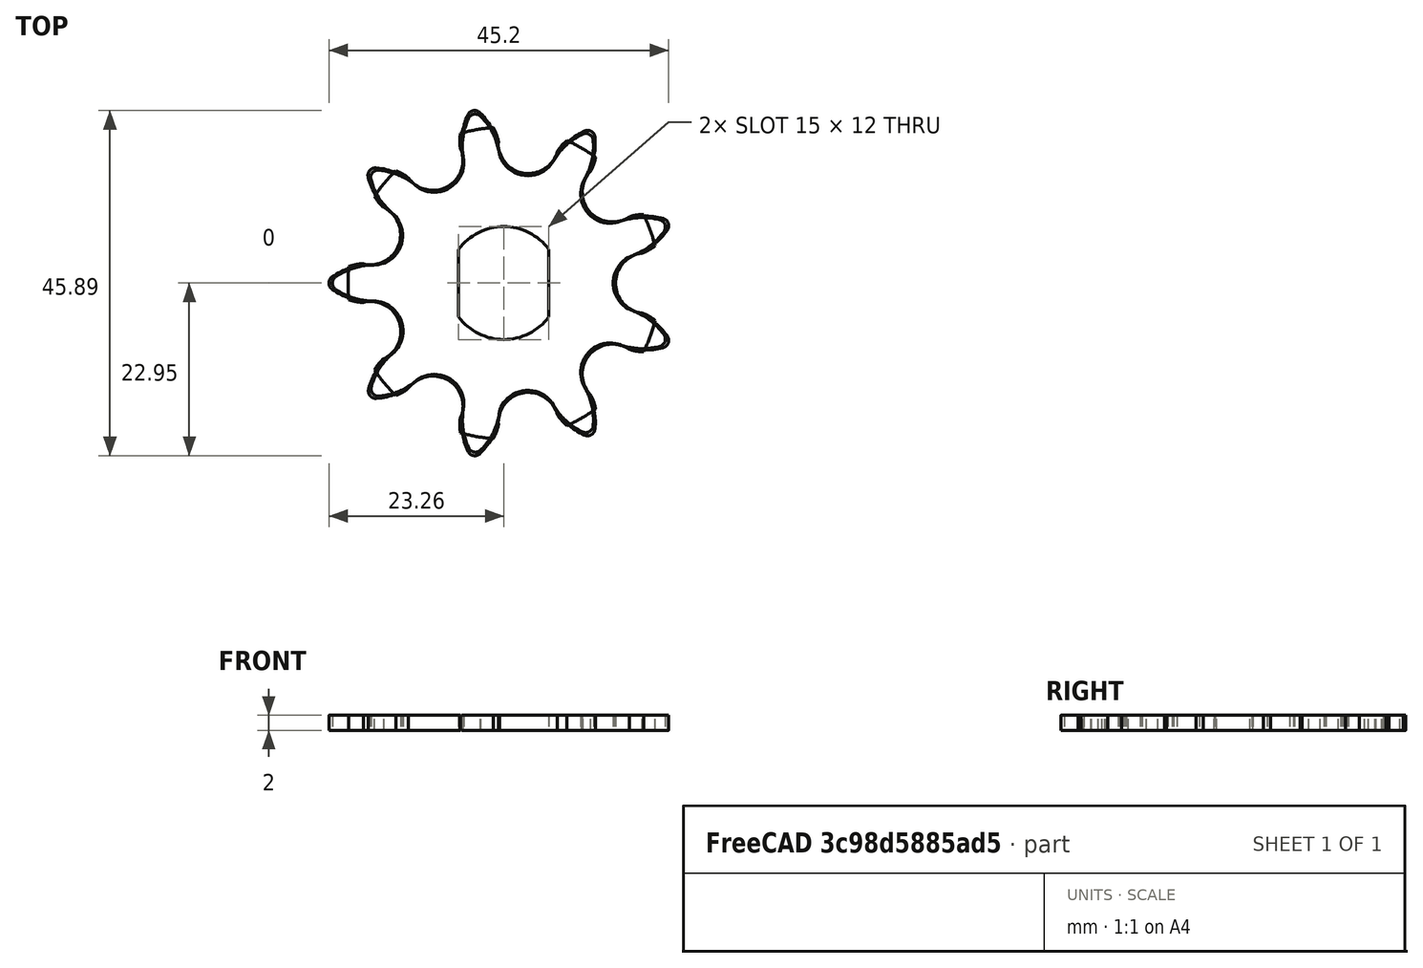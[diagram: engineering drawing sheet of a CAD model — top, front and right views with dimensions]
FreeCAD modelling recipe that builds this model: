
FCSTD DOCUMENT  (FreeCAD 0.21R33771 (Git))
Label: Звезда
License: All rights reserved
LicenseURL: http://en.wikipedia.org/wiki/All_rights_reserved
objects: Part::Cut×4, Part::Box×2, Part::FeaturePython×2, Part::Cylinder×1, Part::MultiFuse×1, Sketcher::SketchObject×1, PartDesign::Pad×1, PartDesign::Body×1, Part::Feature×1
note: 15 computed .brp shape members not serialized (recipe doc carries the construction recipe); baked Part::Feature solids carry a one-line shape summary decoded from their .brp

FEATURE [Part::Cylinder] Cylinder  label="Цилиндр"
  Angle = 360
  AttacherType = Attacher::AttachEngine3D
  FirstAngle = 0
  Height = 2
  Radius = 7.5
  SecondAngle = 0
FEATURE [Part::Box] Box  label="Куб"
  AttacherType = Attacher::AttachEngine3D
  Height = 3
  Length = 2
  Placement = pos=(6,-7.5,0) rot=(0,0,1;0rad)
  Width = 15
FEATURE [Part::Box] Box001  label="Куб001"
  AttacherType = Attacher::AttachEngine3D
  Height = 3
  Length = 2
  Placement = pos=(-8,-7.5,0) rot=(0,0,1;0rad)
  Width = 15
FEATURE [Part::MultiFuse] Fusion
  Refine = true
  Shapes = -> [Box,Box001]
FEATURE [Part::Cut] Cut
  Base = -> Cylinder
  Refine = true
  Tool = -> Fusion
FEATURE [Part::FeaturePython] LanternGear  # WARN: FeaturePython — macro-defined, semantics opaque (R4)
  AttacherType = Attacher::AttachEngine3D
  bolt_radius = 4
  head = -0.5
  height = 2
  module = 4.18
  num_profiles = 10
  teeth = 9
  version = 1.2.0
FEATURE [Part::Cut] Cut001
  Base = -> LanternGear
  Refine = true
  Tool = -> Cut
FEATURE [Sketcher::SketchObject] Sketch
  FullyConstrained = false
  MapMode = 5
  Support = -> [XY_Plane]
  sketch-geometry (36):
    g0: ArcOfCircle CenterX=18.8521 CenterY=-0.00307638 CenterZ=0 NormalX=0 NormalY=0 NormalZ=1 AngleXU=0 Radius=3.99594 StartAngle=1.92021 EndAngle=4.36364
    g1: ArcOfCircle CenterX=14.4427 CenterY=12.1214 CenterZ=0 NormalX=0 NormalY=0 NormalZ=1 AngleXU=0 Radius=3.99956 StartAngle=2.61807 EndAngle=5.06145
    g2: ArcOfCircle CenterX=3.27375 CenterY=18.5664 CenterZ=0 NormalX=0 NormalY=0 NormalZ=1 AngleXU=0 Radius=4.00007 StartAngle=3.31592 EndAngle=5.76013
    g3: ArcOfCircle CenterX=-9.4255 CenterY=16.3265 CenterZ=0 NormalX=0 NormalY=0 NormalZ=1 AngleXU=0 Radius=3.99916 StartAngle=4.01407 EndAngle=6.45773
    g4: ArcOfCircle CenterX=-17.7189 CenterY=6.45012 CenterZ=0 NormalX=0 NormalY=0 NormalZ=1 AngleXU=0 Radius=3.99935 StartAngle=4.71461 EndAngle=7.15498
    g5: ArcOfCircle CenterX=-17.713 CenterY=-6.48365 CenterZ=0 NormalX=0 NormalY=0 NormalZ=1 AngleXU=0 Radius=4.03982 StartAngle=5.41203 EndAngle=7.85425
    g6: ArcOfCircle CenterX=-9.40813 CenterY=-16.3627 CenterZ=0 NormalX=0 NormalY=0 NormalZ=1 AngleXU=0 Radius=3.99368 StartAngle=6.12296 EndAngle=8.55045
    g7: ArcOfCircle CenterX=3.26409 CenterY=-18.5325 CenterZ=0 NormalX=0 NormalY=0 NormalZ=1 AngleXU=0 Radius=3.9982 StartAngle=0.520185 EndAngle=2.87441
    g8: ArcOfCircle CenterX=14.4386 CenterY=-12.1181 CenterZ=0 NormalX=0 NormalY=0 NormalZ=1 AngleXU=0 Radius=4.00046 StartAngle=1.22083 EndAngle=3.66684
    g9: ArcOfCircle CenterX=18.8521 CenterY=-1.6e-15 CenterZ=0 NormalX=0 NormalY=0 NormalZ=1 AngleXU=0 Radius=8.89636 StartAngle=4.36343 EndAngle=4.97952
    g10: ArcOfCircle CenterX=14.4423 CenterY=12.1192 CenterZ=0 NormalX=0 NormalY=0 NormalZ=1 AngleXU=0 Radius=8.9035 StartAngle=5.06105 EndAngle=5.67731
    g11: ArcOfCircle CenterX=3.27349 CenterY=18.5668 CenterZ=0 NormalX=0 NormalY=0 NormalZ=1 AngleXU=0 Radius=8.89593 StartAngle=5.75987 EndAngle=6.37643
    g12: ArcOfCircle CenterX=-9.42653 CenterY=16.3272 CenterZ=0 NormalX=0 NormalY=0 NormalZ=1 AngleXU=0 Radius=8.8961 StartAngle=0.174603 EndAngle=0.781513
    g13: ArcOfCircle CenterX=-17.7173 CenterY=6.44109 CenterZ=0 NormalX=0 NormalY=0 NormalZ=1 AngleXU=0 Radius=8.90336 StartAngle=0.873017 EndAngle=1.48801
    g14: ArcOfCircle CenterX=-17.6902 CenterY=-6.46089 CenterZ=0 NormalX=0 NormalY=0 NormalZ=1 AngleXU=0 Radius=8.91169 StartAngle=1.57302 EndAngle=2.18686
    g15: ArcOfCircle CenterX=-9.39599 CenterY=-16.3607 CenterZ=0 NormalX=0 NormalY=0 NormalZ=1 AngleXU=0 Radius=8.87254 StartAngle=2.27075 EndAngle=2.88286
    g16: ArcOfCircle CenterX=3.28393 CenterY=-18.5776 CenterZ=0 NormalX=0 NormalY=0 NormalZ=1 AngleXU=0 Radius=8.89064 StartAngle=2.96319 EndAngle=3.58322
    g17: ArcOfCircle CenterX=14.4506 CenterY=-12.1215 CenterZ=0 NormalX=0 NormalY=0 NormalZ=1 AngleXU=0 Radius=8.89511 StartAngle=3.6621 EndAngle=4.27987
    g18: ArcOfCircle CenterX=-17.7165 CenterY=6.44925 CenterZ=0 NormalX=0 NormalY=0 NormalZ=1 AngleXU=0 Radius=8.89308 StartAngle=4.09873 EndAngle=4.71266
    g19: ArcOfCircle CenterX=-9.42653 CenterY=16.3272 CenterZ=0 NormalX=0 NormalY=0 NormalZ=1 AngleXU=0 Radius=8.8972 StartAngle=3.39892 EndAngle=4.01426
    g20: ArcOfCircle CenterX=3.27349 CenterY=18.5668 CenterZ=0 NormalX=0 NormalY=0 NormalZ=1 AngleXU=0 Radius=8.89593 StartAngle=2.70052 EndAngle=3.31624
    g21: ArcOfCircle CenterX=14.4423 CenterY=12.1192 CenterZ=0 NormalX=0 NormalY=0 NormalZ=1 AngleXU=0 Radius=8.89579 StartAngle=2.0205 EndAngle=2.61784
    g22: ArcOfCircle CenterX=18.8521 CenterY=1.2e-15 CenterZ=0 NormalX=0 NormalY=0 NormalZ=1 AngleXU=0 Radius=8.89894 StartAngle=1.30342 EndAngle=1.91961
    g23: ArcOfCircle CenterX=14.4506 CenterY=-12.1215 CenterZ=0 NormalX=0 NormalY=0 NormalZ=1 AngleXU=0 Radius=8.89704 StartAngle=0.607101 EndAngle=1.22256
    g24: ArcOfCircle CenterX=3.28393 CenterY=-18.5776 CenterZ=0 NormalX=0 NormalY=0 NormalZ=1 AngleXU=0 Radius=8.88949 StartAngle=6.19282 EndAngle=6.80792
    g25: ArcOfCircle CenterX=-9.39599 CenterY=-16.3607 CenterZ=0 NormalX=0 NormalY=0 NormalZ=1 AngleXU=0 Radius=8.87421 StartAngle=5.49392 EndAngle=6.15708
    g26: ArcOfCircle CenterX=-17.6902 CenterY=-6.46089 CenterZ=0 NormalX=0 NormalY=0 NormalZ=1 AngleXU=0 Radius=8.91523 StartAngle=4.79888 EndAngle=5.40899
    g27: ArcOfCircle CenterX=-17.0637 CenterY=14.3174 CenterZ=0 NormalX=0 NormalY=0 NormalZ=1 AngleXU=0 Radius=1 StartAngle=1.48801 EndAngle=3.39892
    g28: ArcOfCircle CenterX=-3.86675 CenterY=21.9376 CenterZ=0 NormalX=0 NormalY=0 NormalZ=1 AngleXU=0 Radius=1 StartAngle=0.714992 EndAngle=2.70052
    g29: ArcOfCircle CenterX=11.1351 CenterY=19.3019 CenterZ=0 NormalX=0 NormalY=0 NormalZ=1 AngleXU=0 Radius=1 StartAngle=0.0932401 EndAngle=2.16499
    g30: ArcOfCircle CenterX=20.939 CenterY=7.61827 CenterZ=0 NormalX=0 NormalY=0 NormalZ=1 AngleXU=0 Radius=1 StartAngle=5.67731 EndAngle=7.58661
    g31: ArcOfCircle CenterX=20.9364 CenterY=-7.6163 CenterZ=0 NormalX=0 NormalY=0 NormalZ=1 AngleXU=0 Radius=1 StartAngle=4.97952 EndAngle=6.89029
    g32: ArcOfCircle CenterX=11.1412 CenterY=-19.2895 CenterZ=0 NormalX=0 NormalY=0 NormalZ=1 AngleXU=0 Radius=1 StartAngle=4.27987 EndAngle=6.19282
    g33: ArcOfCircle CenterX=-3.84965 CenterY=-21.9501 CenterZ=0 NormalX=0 NormalY=0 NormalZ=1 AngleXU=0 Radius=1 StartAngle=3.58322 EndAngle=5.49392
    g34: ArcOfCircle CenterX=-17.0065 CenterY=-14.3465 CenterZ=0 NormalX=0 NormalY=0 NormalZ=1 AngleXU=0 Radius=1 StartAngle=2.88286 EndAngle=4.79888
    g35: ArcOfCircle CenterX=-22.2618 CenterY=-0.00369913 CenterZ=0 NormalX=0 NormalY=0 NormalZ=1 AngleXU=0 Radius=1 StartAngle=2.18686 EndAngle=4.09873
  constraints (44):
    c: Coincident(g0,g23)
    c: Coincident(g8,g9)
    c: Coincident(g8,g24)
    c: Coincident(g7,g17)
    c: Coincident(g7,g25)
    c: Coincident(g6,g16)
    c: Coincident(g6,g26)
    c: Coincident(g5,g15)
    c: Coincident(g5,g18)
    c: Coincident(g4,g14)
    c: Coincident(g4,g19)
    c: Coincident(g3,g13)
    c: Coincident(g3,g20)
    c: Coincident(g2,g12)
    c: Coincident(g2,g21)
    c: Coincident(g1,g11)
    c: Coincident(g1,g22)
    c: Coincident(g0,g10)
    c: Diameter(g27) = 2
    c: Equal(g27,g28) = 2
    c: Tangent(g27,g19) = -1.5708
    c: Tangent(g27,g13) = -1.5708
    c: Tangent(g28,g20) = -1.5708
    c: Coincident(g28,g12)
    c: Coincident(g29,g21)
    c: Tangent(g11,g29) = -1.5708
    c: Diameter(g30) = 2
    c: Equal(g30,g31) = 2
    c: Equal(g30,g32) = 2
    c: Equal(g30,g33) = 2
    c: Equal(g30,g34) = 2
    c: Equal(g30,g35) = 2
    c: Tangent(g35,g18) = -1.5708
    c: Tangent(g35,g14) = -1.5708
    c: Tangent(g34,g26) = -1.5708
    c: Tangent(g34,g15) = -1.5708
    c: Tangent(g33,g25) = -1.5708
    c: Tangent(g33,g16) = -1.5708
    c: Tangent(g32,g24) = -1.5708
    c: Tangent(g32,g17) = -1.5708
    c: Tangent(g31,g23) = -1.5708
    c: Tangent(g31,g9) = -1.5708
    c: Tangent(g10,g30) = -1.5708
    c: Tangent(g22,g30) = -1.5708
FEATURE [PartDesign::Pad] Pad
  Direction = (0,0,1)
  Length = 2
  Length2 = 10
  Profile = -> Sketch
  ReferenceAxis = -> Sketch [N_Axis]
  Refine = true
  Type = 0
FEATURE [PartDesign::Body] Body
  Group = -> [Sketch,Pad]
  Origin = -> Origin
  Tip = -> Pad
FEATURE [Part::Cut] Cut002
  Base = -> Body
  Refine = true
  Tool = -> Cut
FEATURE [Part::Feature] Body001
  shape: bbox 45.2 x 45.89 x 2 mm, 38 faces (baked)
FEATURE [Part::FeaturePython] Clone  label="Body002"  # Draft clone (typed FeaturePython)
  AttacherType = Attacher::AttachEngine3D
  Fuse = false
  Objects = -> [Body001]
  Scale = (0.98,0.98,1)
FEATURE [Part::Cut] Cut003
  Base = -> Clone
  Refine = true
  Tool = -> Cut
